# Revit family: Shower_Arm-DXV-357023XX_Series
name_source: partatom
category: Plumbing Fixtures
units: mm (PartAtom-declared; Revit-internal decimal feet)

## family parameters
Always vertical = No
Cut with Voids When Loaded = No
OmniClass Number = 23.45.05.14.17
OmniClass Title = Showers
Part Type = Normal
Room Calculation Point = No
Round Connector Dimension = Use Diameter
Shared = Yes
Work Plane-Based = Yes

## types (6) — shared parameters
Assembly Code = D2010710
CW Connection = No
CWFU = 3
Default Elevation = 0"
Description = Ceiling Mount Shower Arm
HW Connection = No
HWFU = 3
Installation Type = Ceiling-Mount
Length = 2 1/8"
Manufacturer = DXV
Price = Prices may vary. Please consult Manufacturer Representative for most up-to-date price list.
Product Documentation Link = https://dxv01.blob.core.windows.net
Product Page URL = https://www.dxv.com
Revised Date = 02/04/2022
Tempered Connection Diameter = 1/2"
Tempered Connection Radius = 1/4"
Tempered Water Connection = Yes
URL = https://www.dxv.com
Vent Connection = No
WFU = 4
Warranty Documentation Link = https://www.dxv.com
Waste Connection = No
Width = 2 1/8"

## per-type parameters (varying)
| type | Finish | Height | Material |
| D35702306.100 | Metal-DXV-100-Polished Chrome | 6" | Metal-DXV-100-Polished Chrome |
| D35702306.144 | Metal-DXV-144-Brushed Nickel | 6" | Metal-DXV-144-Brushed Nickel |
| D35702306.150 | Metal-DXV-150-Platinum Nickel | 6" | Metal-DXV-150-Platinum Nickel |
| D35702312.100 | Metal-DXV-100-Polished Chrome | 12" | Metal-DXV-100-Polished Chrome |
| D35702312.144 | Metal-DXV-144-Brushed Nickel | 12" | Metal-DXV-144-Brushed Nickel |
| D35702312.150 | Metal-DXV-150-Platinum Nickel | 12" | Metal-DXV-150-Platinum Nickel |

note: column(s) folded — value = type name in every type: Model

## geometry (parser evidence)
native form markers: Sweep x3
no freeform markers — native parametric forms only
